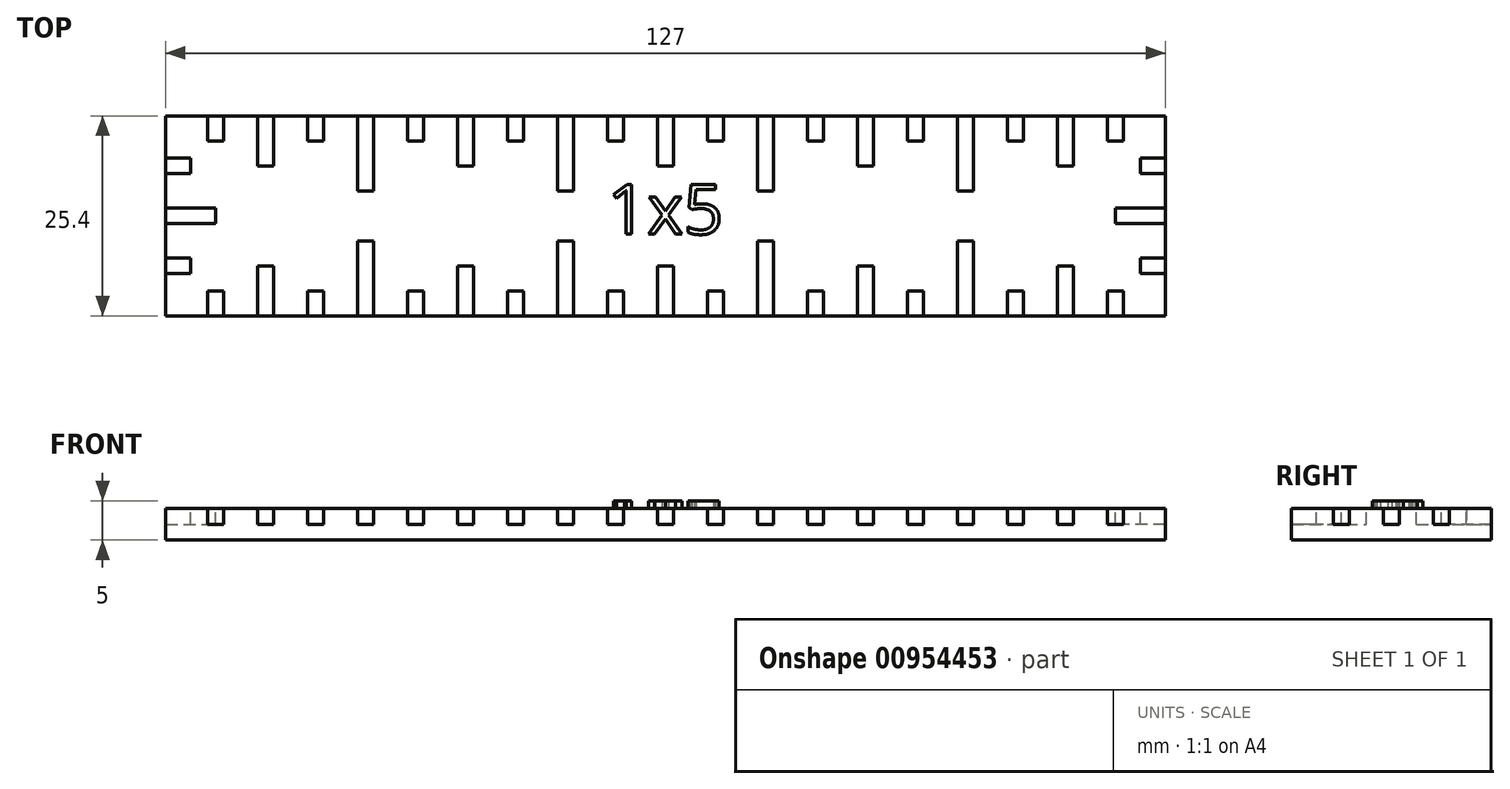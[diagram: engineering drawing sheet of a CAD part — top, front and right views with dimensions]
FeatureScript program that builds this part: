
annotation { "Feature Type Name" : "Feature", "Feature Type Description" : "" }
export const myFeature = defineFeature(function(context is Context, id is Id, definition is map)
    precondition{}
    {
        {
            var Q0;
            Q0=qCreatedBy(makeId("Top.planeOp"),FACE);
            var sketch = newSketch(context, id + "F0", { "sketchPlane" : qUnion([Q0])});
            skLineSegment(sketch, "E0.bottom", {"start": v(-63.5, 12.7) * mm, "end": v(63.5, 12.7) * mm});
            skLineSegment(sketch, "E0.top", {"start": v(-63.5, -12.7) * mm, "end": v(63.5, -12.7) * mm});
            skLineSegment(sketch, "E0.left", {"start": v(-63.5, 12.7) * mm, "end": v(-63.5, -12.7) * mm});
            skLineSegment(sketch, "E0.right", {"start": v(63.5, 12.7) * mm, "end": v(63.5, -12.7) * mm});
            skPoint(sketch, "E0.middle", {"position": v(0, 0) * mm});
            skSolve(sketch);
        }
        {
            var Q0;
            Q0=makeQuery(id+"F0.imprint","IMPRINT",FACE,{"disambiguationData":[TD([[makeQuery(id+"F0.imprint","IMPRINT",EDGE,{"derivedFrom":sQuery(id+"F0.wireOp",EDGE,"E0.bottom")}),-1.0]])]});
            extrude(context, id + "F1", {"entities" : qUnion([Q0]), "depth" : 4 * mm, "offsetDistance" : 25 * mm});
        }
        {
            var Q0;
            Q0=makeQuery(id+"F1.opExtrude","CAP_FACE",FACE,{"disambiguationData":[OSD([sQuery(id+"F0.wireOp",EDGE,"E0.bottom"),sQuery(id+"F0.wireOp",EDGE,"E0.top"),sQuery(id+"F0.wireOp",EDGE,"E0.left"),sQuery(id+"F0.wireOp",EDGE,"E0.right")])],"isStart":false});
            var sketch = newSketch(context, id + "F2", { "sketchPlane" : qUnion([Q0])});
            skLineSegment(sketch, "E1.bottom", {"start": v(-1, -6.35) * mm, "end": v(1, -6.35) * mm});
            skLineSegment(sketch, "E1.top", {"start": v(-1, -19.05) * mm, "end": v(1, -19.05) * mm});
            skLineSegment(sketch, "E1.left", {"start": v(-1, -6.35) * mm, "end": v(-1, -19.05) * mm});
            skLineSegment(sketch, "E1.right", {"start": v(1, -6.35) * mm, "end": v(1, -19.05) * mm});
            skPoint(sketch, "E1.middle", {"position": v(0, -12.7) * mm});
            skLineSegment(sketch, "E2.bottom", {"start": v(5.35, -9.53) * mm, "end": v(7.35, -9.53) * mm});
            skLineSegment(sketch, "E2.top", {"start": v(5.35, -15.88) * mm, "end": v(7.35, -15.88) * mm});
            skLineSegment(sketch, "E2.left", {"start": v(5.35, -9.53) * mm, "end": v(5.35, -15.88) * mm});
            skLineSegment(sketch, "E2.right", {"start": v(7.35, -9.53) * mm, "end": v(7.35, -15.88) * mm});
            skPoint(sketch, "E2.middle", {"position": v(6.35, -12.7) * mm});
            skLineSegment(sketch, "E3.bottom", {"start": v(-7.35, -9.53) * mm, "end": v(-5.35, -9.53) * mm});
            skLineSegment(sketch, "E3.top", {"start": v(-7.35, -15.88) * mm, "end": v(-5.35, -15.88) * mm});
            skLineSegment(sketch, "E3.left", {"start": v(-7.35, -9.53) * mm, "end": v(-7.35, -15.88) * mm});
            skLineSegment(sketch, "E3.right", {"start": v(-5.35, -9.53) * mm, "end": v(-5.35, -15.88) * mm});
            skPoint(sketch, "E3.middle", {"position": v(-6.35, -12.7) * mm});
            skLineSegment(sketch, "E4.bottom", {"start": v(-69.85, -1) * mm, "end": v(-69.85, 1) * mm});
            skLineSegment(sketch, "E4.top", {"start": v(-57.15, -1) * mm, "end": v(-57.15, 1) * mm});
            skLineSegment(sketch, "E4.left", {"start": v(-69.85, -1) * mm, "end": v(-57.15, -1) * mm});
            skLineSegment(sketch, "E4.right", {"start": v(-69.85, 1) * mm, "end": v(-57.15, 1) * mm});
            skPoint(sketch, "E4.middle", {"position": v(-63.5, 0) * mm});
            skLineSegment(sketch, "E5.bottom", {"start": v(-66.68, 5.35) * mm, "end": v(-66.68, 7.35) * mm});
            skLineSegment(sketch, "E5.top", {"start": v(-60.33, 5.35) * mm, "end": v(-60.33, 7.35) * mm});
            skLineSegment(sketch, "E5.left", {"start": v(-66.68, 5.35) * mm, "end": v(-60.33, 5.35) * mm});
            skLineSegment(sketch, "E5.right", {"start": v(-66.68, 7.35) * mm, "end": v(-60.33, 7.35) * mm});
            skPoint(sketch, "E5.middle", {"position": v(-63.5, 6.35) * mm});
            skLineSegment(sketch, "E6.bottom", {"start": v(-66.68, -7.35) * mm, "end": v(-66.68, -5.35) * mm});
            skLineSegment(sketch, "E6.top", {"start": v(-60.33, -7.35) * mm, "end": v(-60.33, -5.35) * mm});
            skLineSegment(sketch, "E6.left", {"start": v(-66.68, -7.35) * mm, "end": v(-60.33, -7.35) * mm});
            skLineSegment(sketch, "E6.right", {"start": v(-66.68, -5.35) * mm, "end": v(-60.33, -5.35) * mm});
            skPoint(sketch, "E6.middle", {"position": v(-63.5, -6.35) * mm});
            skLineSegment(sketch, "E7.bottom", {"start": v(1, 6.35) * mm, "end": v(-1, 6.35) * mm});
            skLineSegment(sketch, "E7.top", {"start": v(1, 19.05) * mm, "end": v(-1, 19.05) * mm});
            skLineSegment(sketch, "E7.left", {"start": v(1, 6.35) * mm, "end": v(1, 19.05) * mm});
            skLineSegment(sketch, "E7.right", {"start": v(-1, 6.35) * mm, "end": v(-1, 19.05) * mm});
            skPoint(sketch, "E7.middle", {"position": v(0, 12.7) * mm});
            skLineSegment(sketch, "E8.bottom", {"start": v(-5.35, 9.53) * mm, "end": v(-7.35, 9.53) * mm});
            skLineSegment(sketch, "E8.top", {"start": v(-5.35, 15.88) * mm, "end": v(-7.35, 15.88) * mm});
            skLineSegment(sketch, "E8.left", {"start": v(-5.35, 9.53) * mm, "end": v(-5.35, 15.88) * mm});
            skLineSegment(sketch, "E8.right", {"start": v(-7.35, 9.53) * mm, "end": v(-7.35, 15.88) * mm});
            skPoint(sketch, "E8.middle", {"position": v(-6.35, 12.7) * mm});
            skLineSegment(sketch, "E9.bottom", {"start": v(7.35, 9.52) * mm, "end": v(5.35, 9.52) * mm});
            skLineSegment(sketch, "E9.top", {"start": v(7.35, 15.88) * mm, "end": v(5.35, 15.88) * mm});
            skLineSegment(sketch, "E9.left", {"start": v(7.35, 9.52) * mm, "end": v(7.35, 15.88) * mm});
            skLineSegment(sketch, "E9.right", {"start": v(5.35, 9.52) * mm, "end": v(5.35, 15.88) * mm});
            skPoint(sketch, "E9.middle", {"position": v(6.35, 12.7) * mm});
            skLineSegment(sketch, "E10.bottom", {"start": v(69.85, 1) * mm, "end": v(69.85, -1) * mm});
            skLineSegment(sketch, "E10.top", {"start": v(57.15, 1) * mm, "end": v(57.15, -1) * mm});
            skLineSegment(sketch, "E10.left", {"start": v(69.85, 1) * mm, "end": v(57.15, 1) * mm});
            skLineSegment(sketch, "E10.right", {"start": v(69.85, -1) * mm, "end": v(57.15, -1) * mm});
            skPoint(sketch, "E10.middle", {"position": v(63.5, 0) * mm});
            skLineSegment(sketch, "E11.bottom", {"start": v(66.68, -5.35) * mm, "end": v(66.68, -7.35) * mm});
            skLineSegment(sketch, "E11.top", {"start": v(60.33, -5.35) * mm, "end": v(60.33, -7.35) * mm});
            skLineSegment(sketch, "E11.left", {"start": v(66.68, -5.35) * mm, "end": v(60.33, -5.35) * mm});
            skLineSegment(sketch, "E11.right", {"start": v(66.68, -7.35) * mm, "end": v(60.33, -7.35) * mm});
            skPoint(sketch, "E11.middle", {"position": v(63.5, -6.35) * mm});
            skLineSegment(sketch, "E12.bottom", {"start": v(66.68, 7.35) * mm, "end": v(66.68, 5.35) * mm});
            skLineSegment(sketch, "E12.top", {"start": v(60.33, 7.35) * mm, "end": v(60.33, 5.35) * mm});
            skLineSegment(sketch, "E12.left", {"start": v(66.68, 7.35) * mm, "end": v(60.33, 7.35) * mm});
            skLineSegment(sketch, "E12.right", {"start": v(66.68, 5.35) * mm, "end": v(60.33, 5.35) * mm});
            skPoint(sketch, "E12.middle", {"position": v(63.5, 6.35) * mm});
            skLineSegment(sketch, "E13.bottom", {"start": v(-11.7, 3.18) * mm, "end": v(-13.7, 3.18) * mm});
            skLineSegment(sketch, "E13.top", {"start": v(-11.7, 22.23) * mm, "end": v(-13.7, 22.23) * mm});
            skLineSegment(sketch, "E13.left", {"start": v(-11.7, 3.18) * mm, "end": v(-11.7, 22.23) * mm});
            skLineSegment(sketch, "E13.right", {"start": v(-13.7, 3.18) * mm, "end": v(-13.7, 22.23) * mm});
            skPoint(sketch, "E13.middle", {"position": v(-12.7, 12.7) * mm});
            skLineSegment(sketch, "E14.bottom", {"start": v(-18.05, 9.53) * mm, "end": v(-20.05, 9.53) * mm});
            skLineSegment(sketch, "E14.top", {"start": v(-18.05, 15.88) * mm, "end": v(-20.05, 15.88) * mm});
            skLineSegment(sketch, "E14.left", {"start": v(-18.05, 9.53) * mm, "end": v(-18.05, 15.88) * mm});
            skLineSegment(sketch, "E14.right", {"start": v(-20.05, 9.53) * mm, "end": v(-20.05, 15.88) * mm});
            skPoint(sketch, "E14.middle", {"position": v(-19.05, 12.7) * mm});
            skLineSegment(sketch, "E15.bottom", {"start": v(-11.7, -22.23) * mm, "end": v(-13.7, -22.23) * mm});
            skLineSegment(sketch, "E15.top", {"start": v(-11.7, -3.18) * mm, "end": v(-13.7, -3.18) * mm});
            skLineSegment(sketch, "E15.left", {"start": v(-11.7, -22.23) * mm, "end": v(-11.7, -3.18) * mm});
            skLineSegment(sketch, "E15.right", {"start": v(-13.7, -22.23) * mm, "end": v(-13.7, -3.18) * mm});
            skPoint(sketch, "E15.middle", {"position": v(-12.7, -12.7) * mm});
            skLineSegment(sketch, "E16.bottom", {"start": v(-18.05, -15.88) * mm, "end": v(-20.05, -15.88) * mm});
            skLineSegment(sketch, "E16.top", {"start": v(-18.05, -9.53) * mm, "end": v(-20.05, -9.53) * mm});
            skLineSegment(sketch, "E16.left", {"start": v(-18.05, -15.88) * mm, "end": v(-18.05, -9.53) * mm});
            skLineSegment(sketch, "E16.right", {"start": v(-20.05, -15.88) * mm, "end": v(-20.05, -9.53) * mm});
            skPoint(sketch, "E16.middle", {"position": v(-19.05, -12.7) * mm});
            skLineSegment(sketch, "E17.bottom", {"start": v(-5.35, -15.88) * mm, "end": v(-7.35, -15.88) * mm});
            skLineSegment(sketch, "E17.top", {"start": v(-5.35, -9.53) * mm, "end": v(-7.35, -9.53) * mm});
            skLineSegment(sketch, "E17.left", {"start": v(-5.35, -15.88) * mm, "end": v(-5.35, -9.53) * mm});
            skLineSegment(sketch, "E17.right", {"start": v(-7.35, -15.88) * mm, "end": v(-7.35, -9.53) * mm});
            skLineSegment(sketch, "E18.bottom", {"start": v(11.7, -3.18) * mm, "end": v(13.7, -3.18) * mm});
            skLineSegment(sketch, "E18.top", {"start": v(11.7, -22.23) * mm, "end": v(13.7, -22.23) * mm});
            skLineSegment(sketch, "E18.left", {"start": v(11.7, -3.18) * mm, "end": v(11.7, -22.23) * mm});
            skLineSegment(sketch, "E18.right", {"start": v(13.7, -3.18) * mm, "end": v(13.7, -22.23) * mm});
            skPoint(sketch, "E18.middle", {"position": v(12.7, -12.7) * mm});
            skLineSegment(sketch, "E19.bottom", {"start": v(18.05, -9.53) * mm, "end": v(20.05, -9.53) * mm});
            skLineSegment(sketch, "E19.top", {"start": v(18.05, -15.88) * mm, "end": v(20.05, -15.88) * mm});
            skLineSegment(sketch, "E19.left", {"start": v(18.05, -9.53) * mm, "end": v(18.05, -15.88) * mm});
            skLineSegment(sketch, "E19.right", {"start": v(20.05, -9.53) * mm, "end": v(20.05, -15.88) * mm});
            skPoint(sketch, "E19.middle", {"position": v(19.05, -12.7) * mm});
            skLineSegment(sketch, "E20.bottom", {"start": v(11.7, 22.23) * mm, "end": v(13.7, 22.23) * mm});
            skLineSegment(sketch, "E20.top", {"start": v(11.7, 3.18) * mm, "end": v(13.7, 3.18) * mm});
            skLineSegment(sketch, "E20.left", {"start": v(11.7, 22.23) * mm, "end": v(11.7, 3.18) * mm});
            skLineSegment(sketch, "E20.right", {"start": v(13.7, 22.23) * mm, "end": v(13.7, 3.18) * mm});
            skPoint(sketch, "E20.middle", {"position": v(12.7, 12.7) * mm});
            skLineSegment(sketch, "E21.bottom", {"start": v(18.05, 15.88) * mm, "end": v(20.05, 15.88) * mm});
            skLineSegment(sketch, "E21.top", {"start": v(18.05, 9.53) * mm, "end": v(20.05, 9.53) * mm});
            skLineSegment(sketch, "E21.left", {"start": v(18.05, 15.88) * mm, "end": v(18.05, 9.53) * mm});
            skLineSegment(sketch, "E21.right", {"start": v(20.05, 15.88) * mm, "end": v(20.05, 9.53) * mm});
            skPoint(sketch, "E21.middle", {"position": v(19.05, 12.7) * mm});
            skLineSegment(sketch, "E22.bottom", {"start": v(5.35, 15.88) * mm, "end": v(7.35, 15.88) * mm});
            skLineSegment(sketch, "E22.top", {"start": v(5.35, 9.53) * mm, "end": v(7.35, 9.53) * mm});
            skLineSegment(sketch, "E22.left", {"start": v(5.35, 15.88) * mm, "end": v(5.35, 9.53) * mm});
            skLineSegment(sketch, "E22.right", {"start": v(7.35, 15.88) * mm, "end": v(7.35, 9.53) * mm});
            skLineSegment(sketch, "E23.bottom", {"start": v(26.4, 6.35) * mm, "end": v(24.4, 6.35) * mm});
            skLineSegment(sketch, "E23.top", {"start": v(26.4, 19.05) * mm, "end": v(24.4, 19.05) * mm});
            skLineSegment(sketch, "E23.left", {"start": v(26.4, 6.35) * mm, "end": v(26.4, 19.05) * mm});
            skLineSegment(sketch, "E23.right", {"start": v(24.4, 6.35) * mm, "end": v(24.4, 19.05) * mm});
            skPoint(sketch, "E23.middle", {"position": v(25.4, 12.7) * mm});
            skLineSegment(sketch, "E24.bottom", {"start": v(20.05, 9.53) * mm, "end": v(18.05, 9.53) * mm});
            skLineSegment(sketch, "E24.top", {"start": v(20.05, 15.88) * mm, "end": v(18.05, 15.88) * mm});
            skLineSegment(sketch, "E24.left", {"start": v(20.05, 9.53) * mm, "end": v(20.05, 15.88) * mm});
            skLineSegment(sketch, "E24.right", {"start": v(18.05, 9.53) * mm, "end": v(18.05, 15.88) * mm});
            skLineSegment(sketch, "E25.bottom", {"start": v(32.75, 9.52) * mm, "end": v(30.75, 9.52) * mm});
            skLineSegment(sketch, "E25.top", {"start": v(32.75, 15.88) * mm, "end": v(30.75, 15.88) * mm});
            skLineSegment(sketch, "E25.left", {"start": v(32.75, 9.52) * mm, "end": v(32.75, 15.88) * mm});
            skLineSegment(sketch, "E25.right", {"start": v(30.75, 9.52) * mm, "end": v(30.75, 15.88) * mm});
            skPoint(sketch, "E25.middle", {"position": v(31.75, 12.7) * mm});
            skLineSegment(sketch, "E26.bottom", {"start": v(30.75, 15.88) * mm, "end": v(32.75, 15.88) * mm});
            skLineSegment(sketch, "E26.top", {"start": v(30.75, 9.53) * mm, "end": v(32.75, 9.53) * mm});
            skLineSegment(sketch, "E26.left", {"start": v(30.75, 15.88) * mm, "end": v(30.75, 9.53) * mm});
            skLineSegment(sketch, "E26.right", {"start": v(32.75, 15.88) * mm, "end": v(32.75, 9.53) * mm});
            skLineSegment(sketch, "E27.bottom", {"start": v(26.4, -19.05) * mm, "end": v(24.4, -19.05) * mm});
            skLineSegment(sketch, "E27.top", {"start": v(26.4, -6.35) * mm, "end": v(24.4, -6.35) * mm});
            skLineSegment(sketch, "E27.left", {"start": v(26.4, -19.05) * mm, "end": v(26.4, -6.35) * mm});
            skLineSegment(sketch, "E27.right", {"start": v(24.4, -19.05) * mm, "end": v(24.4, -6.35) * mm});
            skPoint(sketch, "E27.middle", {"position": v(25.4, -12.7) * mm});
            skLineSegment(sketch, "E28.bottom", {"start": v(20.05, -15.88) * mm, "end": v(18.05, -15.88) * mm});
            skLineSegment(sketch, "E28.top", {"start": v(20.05, -9.53) * mm, "end": v(18.05, -9.53) * mm});
            skLineSegment(sketch, "E28.left", {"start": v(20.05, -15.88) * mm, "end": v(20.05, -9.52) * mm});
            skLineSegment(sketch, "E28.right", {"start": v(18.05, -15.88) * mm, "end": v(18.05, -9.52) * mm});
            skLineSegment(sketch, "E29.bottom", {"start": v(32.75, -15.88) * mm, "end": v(30.75, -15.88) * mm});
            skLineSegment(sketch, "E29.top", {"start": v(32.75, -9.53) * mm, "end": v(30.75, -9.53) * mm});
            skLineSegment(sketch, "E29.left", {"start": v(32.75, -15.88) * mm, "end": v(32.75, -9.52) * mm});
            skLineSegment(sketch, "E29.right", {"start": v(30.75, -15.88) * mm, "end": v(30.75, -9.52) * mm});
            skPoint(sketch, "E29.middle", {"position": v(31.75, -12.7) * mm});
            skLineSegment(sketch, "E30.bottom", {"start": v(20.05, -15.87) * mm, "end": v(18.05, -15.87) * mm});
            skLineSegment(sketch, "E30.top", {"start": v(20.05, -9.52) * mm, "end": v(18.05, -9.52) * mm});
            skLineSegment(sketch, "E30.left", {"start": v(20.05, -15.87) * mm, "end": v(20.05, -9.52) * mm});
            skLineSegment(sketch, "E30.right", {"start": v(18.05, -15.87) * mm, "end": v(18.05, -9.52) * mm});
            skLineSegment(sketch, "E31.bottom", {"start": v(30.75, -9.52) * mm, "end": v(32.75, -9.52) * mm});
            skLineSegment(sketch, "E31.top", {"start": v(30.75, -15.88) * mm, "end": v(32.75, -15.88) * mm});
            skLineSegment(sketch, "E31.left", {"start": v(30.75, -9.52) * mm, "end": v(30.75, -15.88) * mm});
            skLineSegment(sketch, "E31.right", {"start": v(32.75, -9.52) * mm, "end": v(32.75, -15.88) * mm});
            skLineSegment(sketch, "E32.bottom", {"start": v(-26.4, -6.35) * mm, "end": v(-24.4, -6.35) * mm});
            skLineSegment(sketch, "E32.top", {"start": v(-26.4, -19.05) * mm, "end": v(-24.4, -19.05) * mm});
            skLineSegment(sketch, "E32.left", {"start": v(-26.4, -6.35) * mm, "end": v(-26.4, -19.05) * mm});
            skLineSegment(sketch, "E32.right", {"start": v(-24.4, -6.35) * mm, "end": v(-24.4, -19.05) * mm});
            skPoint(sketch, "E32.middle", {"position": v(-25.4, -12.7) * mm});
            skLineSegment(sketch, "E33.bottom", {"start": v(-20.05, -9.53) * mm, "end": v(-18.05, -9.53) * mm});
            skLineSegment(sketch, "E33.top", {"start": v(-20.05, -15.88) * mm, "end": v(-18.05, -15.88) * mm});
            skLineSegment(sketch, "E33.left", {"start": v(-20.05, -9.53) * mm, "end": v(-20.05, -15.88) * mm});
            skLineSegment(sketch, "E33.right", {"start": v(-18.05, -9.53) * mm, "end": v(-18.05, -15.88) * mm});
            skLineSegment(sketch, "E34.bottom", {"start": v(-32.75, -9.53) * mm, "end": v(-30.75, -9.53) * mm});
            skLineSegment(sketch, "E34.top", {"start": v(-32.75, -15.88) * mm, "end": v(-30.75, -15.88) * mm});
            skLineSegment(sketch, "E34.left", {"start": v(-32.75, -9.53) * mm, "end": v(-32.75, -15.88) * mm});
            skLineSegment(sketch, "E34.right", {"start": v(-30.75, -9.53) * mm, "end": v(-30.75, -15.88) * mm});
            skPoint(sketch, "E34.middle", {"position": v(-31.75, -12.7) * mm});
            skLineSegment(sketch, "E35.bottom", {"start": v(-30.75, -15.88) * mm, "end": v(-32.75, -15.88) * mm});
            skLineSegment(sketch, "E35.top", {"start": v(-30.75, -9.53) * mm, "end": v(-32.75, -9.53) * mm});
            skLineSegment(sketch, "E35.left", {"start": v(-30.75, -15.88) * mm, "end": v(-30.75, -9.53) * mm});
            skLineSegment(sketch, "E35.right", {"start": v(-32.75, -15.88) * mm, "end": v(-32.75, -9.53) * mm});
            skLineSegment(sketch, "E36.bottom", {"start": v(-26.4, 19.05) * mm, "end": v(-24.4, 19.05) * mm});
            skLineSegment(sketch, "E36.top", {"start": v(-26.4, 6.35) * mm, "end": v(-24.4, 6.35) * mm});
            skLineSegment(sketch, "E36.left", {"start": v(-26.4, 19.05) * mm, "end": v(-26.4, 6.35) * mm});
            skLineSegment(sketch, "E36.right", {"start": v(-24.4, 19.05) * mm, "end": v(-24.4, 6.35) * mm});
            skPoint(sketch, "E36.middle", {"position": v(-25.4, 12.7) * mm});
            skLineSegment(sketch, "E37.bottom", {"start": v(-20.05, 15.88) * mm, "end": v(-18.05, 15.88) * mm});
            skLineSegment(sketch, "E37.top", {"start": v(-20.05, 9.53) * mm, "end": v(-18.05, 9.53) * mm});
            skLineSegment(sketch, "E37.left", {"start": v(-20.05, 15.88) * mm, "end": v(-20.05, 9.53) * mm});
            skLineSegment(sketch, "E37.right", {"start": v(-18.05, 15.88) * mm, "end": v(-18.05, 9.53) * mm});
            skLineSegment(sketch, "E38.bottom", {"start": v(-32.75, 15.88) * mm, "end": v(-30.75, 15.88) * mm});
            skLineSegment(sketch, "E38.top", {"start": v(-32.75, 9.53) * mm, "end": v(-30.75, 9.53) * mm});
            skLineSegment(sketch, "E38.left", {"start": v(-32.75, 15.88) * mm, "end": v(-32.75, 9.53) * mm});
            skLineSegment(sketch, "E38.right", {"start": v(-30.75, 15.88) * mm, "end": v(-30.75, 9.53) * mm});
            skPoint(sketch, "E38.middle", {"position": v(-31.75, 12.7) * mm});
            skLineSegment(sketch, "E39.bottom", {"start": v(-30.75, 9.53) * mm, "end": v(-32.75, 9.53) * mm});
            skLineSegment(sketch, "E39.top", {"start": v(-30.75, 15.88) * mm, "end": v(-32.75, 15.88) * mm});
            skLineSegment(sketch, "E39.left", {"start": v(-30.75, 9.53) * mm, "end": v(-30.75, 15.88) * mm});
            skLineSegment(sketch, "E39.right", {"start": v(-32.75, 9.53) * mm, "end": v(-32.75, 15.88) * mm});
            skLineSegment(sketch, "E40.bottom", {"start": v(32.75, 9.53) * mm, "end": v(30.75, 9.53) * mm});
            skLineSegment(sketch, "E40.left", {"start": v(32.75, 9.53) * mm, "end": v(32.75, 15.88) * mm});
            skLineSegment(sketch, "E40.right", {"start": v(30.75, 9.53) * mm, "end": v(30.75, 15.88) * mm});
            skLineSegment(sketch, "E41.bottom", {"start": v(37.1, 22.23) * mm, "end": v(39.1, 22.23) * mm});
            skLineSegment(sketch, "E41.top", {"start": v(37.1, 3.18) * mm, "end": v(39.1, 3.18) * mm});
            skLineSegment(sketch, "E41.left", {"start": v(37.1, 22.23) * mm, "end": v(37.1, 3.18) * mm});
            skLineSegment(sketch, "E41.right", {"start": v(39.1, 22.23) * mm, "end": v(39.1, 3.18) * mm});
            skPoint(sketch, "E41.middle", {"position": v(38.1, 12.7) * mm});
            skLineSegment(sketch, "E42.bottom", {"start": v(43.45, 15.88) * mm, "end": v(45.45, 15.88) * mm});
            skLineSegment(sketch, "E42.top", {"start": v(43.45, 9.53) * mm, "end": v(45.45, 9.53) * mm});
            skLineSegment(sketch, "E42.left", {"start": v(43.45, 15.88) * mm, "end": v(43.45, 9.53) * mm});
            skLineSegment(sketch, "E42.right", {"start": v(45.45, 15.88) * mm, "end": v(45.45, 9.53) * mm});
            skPoint(sketch, "E42.middle", {"position": v(44.45, 12.7) * mm});
            skLineSegment(sketch, "E43.bottom", {"start": v(51.8, 6.35) * mm, "end": v(49.8, 6.35) * mm});
            skLineSegment(sketch, "E43.top", {"start": v(51.8, 19.05) * mm, "end": v(49.8, 19.05) * mm});
            skLineSegment(sketch, "E43.left", {"start": v(51.8, 6.35) * mm, "end": v(51.8, 19.05) * mm});
            skLineSegment(sketch, "E43.right", {"start": v(49.8, 6.35) * mm, "end": v(49.8, 19.05) * mm});
            skPoint(sketch, "E43.middle", {"position": v(50.8, 12.7) * mm});
            skLineSegment(sketch, "E44.bottom", {"start": v(45.45, 9.53) * mm, "end": v(43.45, 9.53) * mm});
            skLineSegment(sketch, "E44.top", {"start": v(45.45, 15.88) * mm, "end": v(43.45, 15.88) * mm});
            skLineSegment(sketch, "E44.left", {"start": v(45.45, 9.53) * mm, "end": v(45.45, 15.88) * mm});
            skLineSegment(sketch, "E44.right", {"start": v(43.45, 9.53) * mm, "end": v(43.45, 15.88) * mm});
            skLineSegment(sketch, "E45.bottom", {"start": v(58.15, 9.53) * mm, "end": v(56.15, 9.53) * mm});
            skLineSegment(sketch, "E45.top", {"start": v(58.15, 15.88) * mm, "end": v(56.15, 15.88) * mm});
            skLineSegment(sketch, "E45.left", {"start": v(58.15, 9.53) * mm, "end": v(58.15, 15.88) * mm});
            skLineSegment(sketch, "E45.right", {"start": v(56.15, 9.53) * mm, "end": v(56.15, 15.88) * mm});
            skPoint(sketch, "E45.middle", {"position": v(57.15, 12.7) * mm});
            skLineSegment(sketch, "E46.bottom", {"start": v(56.15, 15.88) * mm, "end": v(58.15, 15.88) * mm});
            skLineSegment(sketch, "E46.top", {"start": v(56.15, 9.53) * mm, "end": v(58.15, 9.53) * mm});
            skLineSegment(sketch, "E46.left", {"start": v(56.15, 15.88) * mm, "end": v(56.15, 9.53) * mm});
            skLineSegment(sketch, "E46.right", {"start": v(58.15, 15.88) * mm, "end": v(58.15, 9.53) * mm});
            skLineSegment(sketch, "E47.bottom", {"start": v(32.75, -15.87) * mm, "end": v(30.75, -15.87) * mm});
            skLineSegment(sketch, "E47.top", {"start": v(32.75, -9.52) * mm, "end": v(30.75, -9.52) * mm});
            skLineSegment(sketch, "E47.left", {"start": v(32.75, -15.87) * mm, "end": v(32.75, -9.52) * mm});
            skLineSegment(sketch, "E47.right", {"start": v(30.75, -15.87) * mm, "end": v(30.75, -9.52) * mm});
            skLineSegment(sketch, "E48.bottom", {"start": v(37.1, -3.17) * mm, "end": v(39.1, -3.17) * mm});
            skLineSegment(sketch, "E48.top", {"start": v(37.1, -22.22) * mm, "end": v(39.1, -22.22) * mm});
            skLineSegment(sketch, "E48.left", {"start": v(37.1, -3.17) * mm, "end": v(37.1, -22.22) * mm});
            skLineSegment(sketch, "E48.right", {"start": v(39.1, -3.17) * mm, "end": v(39.1, -22.22) * mm});
            skPoint(sketch, "E48.middle", {"position": v(38.1, -12.7) * mm});
            skLineSegment(sketch, "E49.bottom", {"start": v(43.45, -9.52) * mm, "end": v(45.45, -9.52) * mm});
            skLineSegment(sketch, "E49.top", {"start": v(43.45, -15.87) * mm, "end": v(45.45, -15.87) * mm});
            skLineSegment(sketch, "E49.left", {"start": v(43.45, -9.52) * mm, "end": v(43.45, -15.87) * mm});
            skLineSegment(sketch, "E49.right", {"start": v(45.45, -9.52) * mm, "end": v(45.45, -15.87) * mm});
            skPoint(sketch, "E49.middle", {"position": v(44.45, -12.7) * mm});
            skLineSegment(sketch, "E50.top", {"start": v(30.75, -15.87) * mm, "end": v(32.75, -15.87) * mm});
            skLineSegment(sketch, "E50.left", {"start": v(30.75, -9.52) * mm, "end": v(30.75, -15.87) * mm});
            skLineSegment(sketch, "E50.right", {"start": v(32.75, -9.52) * mm, "end": v(32.75, -15.87) * mm});
            skLineSegment(sketch, "E51.bottom", {"start": v(51.8, -19.05) * mm, "end": v(49.8, -19.05) * mm});
            skLineSegment(sketch, "E51.top", {"start": v(51.8, -6.35) * mm, "end": v(49.8, -6.35) * mm});
            skLineSegment(sketch, "E51.left", {"start": v(51.8, -19.05) * mm, "end": v(51.8, -6.35) * mm});
            skLineSegment(sketch, "E51.right", {"start": v(49.8, -19.05) * mm, "end": v(49.8, -6.35) * mm});
            skPoint(sketch, "E51.middle", {"position": v(50.8, -12.7) * mm});
            skLineSegment(sketch, "E52.bottom", {"start": v(45.45, -15.87) * mm, "end": v(43.45, -15.87) * mm});
            skLineSegment(sketch, "E52.top", {"start": v(45.45, -9.52) * mm, "end": v(43.45, -9.52) * mm});
            skLineSegment(sketch, "E52.left", {"start": v(45.45, -15.87) * mm, "end": v(45.45, -9.52) * mm});
            skLineSegment(sketch, "E52.right", {"start": v(43.45, -15.87) * mm, "end": v(43.45, -9.52) * mm});
            skLineSegment(sketch, "E53.bottom", {"start": v(58.15, -15.87) * mm, "end": v(56.15, -15.87) * mm});
            skLineSegment(sketch, "E53.top", {"start": v(58.15, -9.52) * mm, "end": v(56.15, -9.52) * mm});
            skLineSegment(sketch, "E53.left", {"start": v(58.15, -15.87) * mm, "end": v(58.15, -9.52) * mm});
            skLineSegment(sketch, "E53.right", {"start": v(56.15, -15.87) * mm, "end": v(56.15, -9.52) * mm});
            skPoint(sketch, "E53.middle", {"position": v(57.15, -12.7) * mm});
            skLineSegment(sketch, "E54.bottom", {"start": v(56.15, -9.52) * mm, "end": v(58.15, -9.52) * mm});
            skLineSegment(sketch, "E54.top", {"start": v(56.15, -15.87) * mm, "end": v(58.15, -15.87) * mm});
            skLineSegment(sketch, "E54.left", {"start": v(56.15, -9.52) * mm, "end": v(56.15, -15.87) * mm});
            skLineSegment(sketch, "E54.right", {"start": v(58.15, -9.52) * mm, "end": v(58.15, -15.87) * mm});
            skLineSegment(sketch, "E55.bottom", {"start": v(-37.1, -22.23) * mm, "end": v(-39.1, -22.23) * mm});
            skLineSegment(sketch, "E55.top", {"start": v(-37.1, -3.18) * mm, "end": v(-39.1, -3.18) * mm});
            skLineSegment(sketch, "E55.left", {"start": v(-37.1, -22.23) * mm, "end": v(-37.1, -3.18) * mm});
            skLineSegment(sketch, "E55.right", {"start": v(-39.1, -22.23) * mm, "end": v(-39.1, -3.18) * mm});
            skPoint(sketch, "E55.middle", {"position": v(-38.1, -12.7) * mm});
            skLineSegment(sketch, "E56.bottom", {"start": v(-43.45, -15.88) * mm, "end": v(-45.45, -15.88) * mm});
            skLineSegment(sketch, "E56.top", {"start": v(-43.45, -9.53) * mm, "end": v(-45.45, -9.53) * mm});
            skLineSegment(sketch, "E56.left", {"start": v(-43.45, -15.88) * mm, "end": v(-43.45, -9.53) * mm});
            skLineSegment(sketch, "E56.right", {"start": v(-45.45, -15.88) * mm, "end": v(-45.45, -9.53) * mm});
            skPoint(sketch, "E56.middle", {"position": v(-44.45, -12.7) * mm});
            skLineSegment(sketch, "E57.bottom", {"start": v(-51.8, -6.35) * mm, "end": v(-49.8, -6.35) * mm});
            skLineSegment(sketch, "E57.top", {"start": v(-51.8, -19.05) * mm, "end": v(-49.8, -19.05) * mm});
            skLineSegment(sketch, "E57.left", {"start": v(-51.8, -6.35) * mm, "end": v(-51.8, -19.05) * mm});
            skLineSegment(sketch, "E57.right", {"start": v(-49.8, -6.35) * mm, "end": v(-49.8, -19.05) * mm});
            skPoint(sketch, "E57.middle", {"position": v(-50.8, -12.7) * mm});
            skLineSegment(sketch, "E58.bottom", {"start": v(-45.45, -9.53) * mm, "end": v(-43.45, -9.53) * mm});
            skLineSegment(sketch, "E58.top", {"start": v(-45.45, -15.88) * mm, "end": v(-43.45, -15.88) * mm});
            skLineSegment(sketch, "E58.left", {"start": v(-45.45, -9.53) * mm, "end": v(-45.45, -15.88) * mm});
            skLineSegment(sketch, "E58.right", {"start": v(-43.45, -9.53) * mm, "end": v(-43.45, -15.88) * mm});
            skLineSegment(sketch, "E59.bottom", {"start": v(-58.15, -9.53) * mm, "end": v(-56.15, -9.53) * mm});
            skLineSegment(sketch, "E59.top", {"start": v(-58.15, -15.88) * mm, "end": v(-56.15, -15.88) * mm});
            skLineSegment(sketch, "E59.left", {"start": v(-58.15, -9.53) * mm, "end": v(-58.15, -15.88) * mm});
            skLineSegment(sketch, "E59.right", {"start": v(-56.15, -9.53) * mm, "end": v(-56.15, -15.88) * mm});
            skPoint(sketch, "E59.middle", {"position": v(-57.15, -12.7) * mm});
            skLineSegment(sketch, "E60.bottom", {"start": v(-56.15, -15.88) * mm, "end": v(-58.15, -15.88) * mm});
            skLineSegment(sketch, "E60.top", {"start": v(-56.15, -9.53) * mm, "end": v(-58.15, -9.53) * mm});
            skLineSegment(sketch, "E60.left", {"start": v(-56.15, -15.88) * mm, "end": v(-56.15, -9.53) * mm});
            skLineSegment(sketch, "E60.right", {"start": v(-58.15, -15.88) * mm, "end": v(-58.15, -9.53) * mm});
            skLineSegment(sketch, "E61.bottom", {"start": v(-32.75, 15.87) * mm, "end": v(-30.75, 15.87) * mm});
            skLineSegment(sketch, "E61.top", {"start": v(-32.75, 9.52) * mm, "end": v(-30.75, 9.52) * mm});
            skLineSegment(sketch, "E61.left", {"start": v(-32.75, 15.87) * mm, "end": v(-32.75, 9.52) * mm});
            skLineSegment(sketch, "E61.right", {"start": v(-30.75, 15.87) * mm, "end": v(-30.75, 9.52) * mm});
            skLineSegment(sketch, "E62.bottom", {"start": v(-37.1, 3.17) * mm, "end": v(-39.1, 3.17) * mm});
            skLineSegment(sketch, "E62.top", {"start": v(-37.1, 22.22) * mm, "end": v(-39.1, 22.22) * mm});
            skLineSegment(sketch, "E62.left", {"start": v(-37.1, 3.17) * mm, "end": v(-37.1, 22.22) * mm});
            skLineSegment(sketch, "E62.right", {"start": v(-39.1, 3.17) * mm, "end": v(-39.1, 22.22) * mm});
            skPoint(sketch, "E62.middle", {"position": v(-38.1, 12.7) * mm});
            skLineSegment(sketch, "E63.bottom", {"start": v(-43.45, 9.52) * mm, "end": v(-45.45, 9.52) * mm});
            skLineSegment(sketch, "E63.top", {"start": v(-43.45, 15.87) * mm, "end": v(-45.45, 15.87) * mm});
            skLineSegment(sketch, "E63.left", {"start": v(-43.45, 9.52) * mm, "end": v(-43.45, 15.87) * mm});
            skLineSegment(sketch, "E63.right", {"start": v(-45.45, 9.52) * mm, "end": v(-45.45, 15.87) * mm});
            skPoint(sketch, "E63.middle", {"position": v(-44.45, 12.7) * mm});
            skLineSegment(sketch, "E64.bottom", {"start": v(-30.75, 9.52) * mm, "end": v(-32.75, 9.52) * mm});
            skLineSegment(sketch, "E64.top", {"start": v(-30.75, 15.87) * mm, "end": v(-32.75, 15.87) * mm});
            skLineSegment(sketch, "E64.left", {"start": v(-30.75, 9.52) * mm, "end": v(-30.75, 15.87) * mm});
            skLineSegment(sketch, "E64.right", {"start": v(-32.75, 9.52) * mm, "end": v(-32.75, 15.87) * mm});
            skLineSegment(sketch, "E65.bottom", {"start": v(-51.8, 19.05) * mm, "end": v(-49.8, 19.05) * mm});
            skLineSegment(sketch, "E65.top", {"start": v(-51.8, 6.35) * mm, "end": v(-49.8, 6.35) * mm});
            skLineSegment(sketch, "E65.left", {"start": v(-51.8, 19.05) * mm, "end": v(-51.8, 6.35) * mm});
            skLineSegment(sketch, "E65.right", {"start": v(-49.8, 19.05) * mm, "end": v(-49.8, 6.35) * mm});
            skPoint(sketch, "E65.middle", {"position": v(-50.8, 12.7) * mm});
            skLineSegment(sketch, "E66.bottom", {"start": v(-45.45, 15.87) * mm, "end": v(-43.45, 15.87) * mm});
            skLineSegment(sketch, "E66.top", {"start": v(-45.45, 9.52) * mm, "end": v(-43.45, 9.52) * mm});
            skLineSegment(sketch, "E66.left", {"start": v(-45.45, 15.87) * mm, "end": v(-45.45, 9.52) * mm});
            skLineSegment(sketch, "E66.right", {"start": v(-43.45, 15.87) * mm, "end": v(-43.45, 9.52) * mm});
            skLineSegment(sketch, "E67.bottom", {"start": v(-58.15, 15.87) * mm, "end": v(-56.15, 15.87) * mm});
            skLineSegment(sketch, "E67.top", {"start": v(-58.15, 9.52) * mm, "end": v(-56.15, 9.52) * mm});
            skLineSegment(sketch, "E67.left", {"start": v(-58.15, 15.87) * mm, "end": v(-58.15, 9.52) * mm});
            skLineSegment(sketch, "E67.right", {"start": v(-56.15, 15.87) * mm, "end": v(-56.15, 9.52) * mm});
            skPoint(sketch, "E67.middle", {"position": v(-57.15, 12.7) * mm});
            skLineSegment(sketch, "E68.bottom", {"start": v(-56.15, 9.52) * mm, "end": v(-58.15, 9.52) * mm});
            skLineSegment(sketch, "E68.top", {"start": v(-56.15, 15.87) * mm, "end": v(-58.15, 15.87) * mm});
            skLineSegment(sketch, "E68.left", {"start": v(-56.15, 9.52) * mm, "end": v(-56.15, 15.87) * mm});
            skLineSegment(sketch, "E68.right", {"start": v(-58.15, 9.52) * mm, "end": v(-58.15, 15.87) * mm});
            skSolve(sketch);
        }
        {
            var Q0;
            Q0=qSketchRegion(id+"F2",true);
            extrude(context, id + "F3", {"entities" : qUnion([Q0]), "operationType" : NewBodyOperationType.REMOVE, "oppositeDirection" : true, "depth" : 2 * mm, "offsetDistance" : 25 * mm});
        }
        {
            var Q0;
            Q0=makeQuery(id+"F1.opExtrude","CAP_FACE",FACE,{"disambiguationData":[OSD([sQuery(id+"F0.wireOp",EDGE,"E0.bottom"),sQuery(id+"F0.wireOp",EDGE,"E0.top"),sQuery(id+"F0.wireOp",EDGE,"E0.left"),sQuery(id+"F0.wireOp",EDGE,"E0.right")])],"isStart":false});
            var sketch = newSketch(context, id + "F4", { "sketchPlane" : qUnion([Q0])});
            skText(sketch, "E69", { "text": "1x5", "fontName": "OpenSans-Regular.ttf"});
            const initialGuessF4  = {"E69": [-0.0074, -0.00233, 1, 0, 0.00636]};
            skSetInitialGuess(sketch, initialGuessF4);
            skSolve(sketch);
        }
        {
            var Q0;
            Q0 = qSketchRegion(id + "F4", true);
            extrude(context, id + "F5", {"entities" : qUnion([Q0]), "operationType" : NewBodyOperationType.ADD, "depth" : 1 * mm, "offsetDistance" : 25 * mm});
        }
    });
